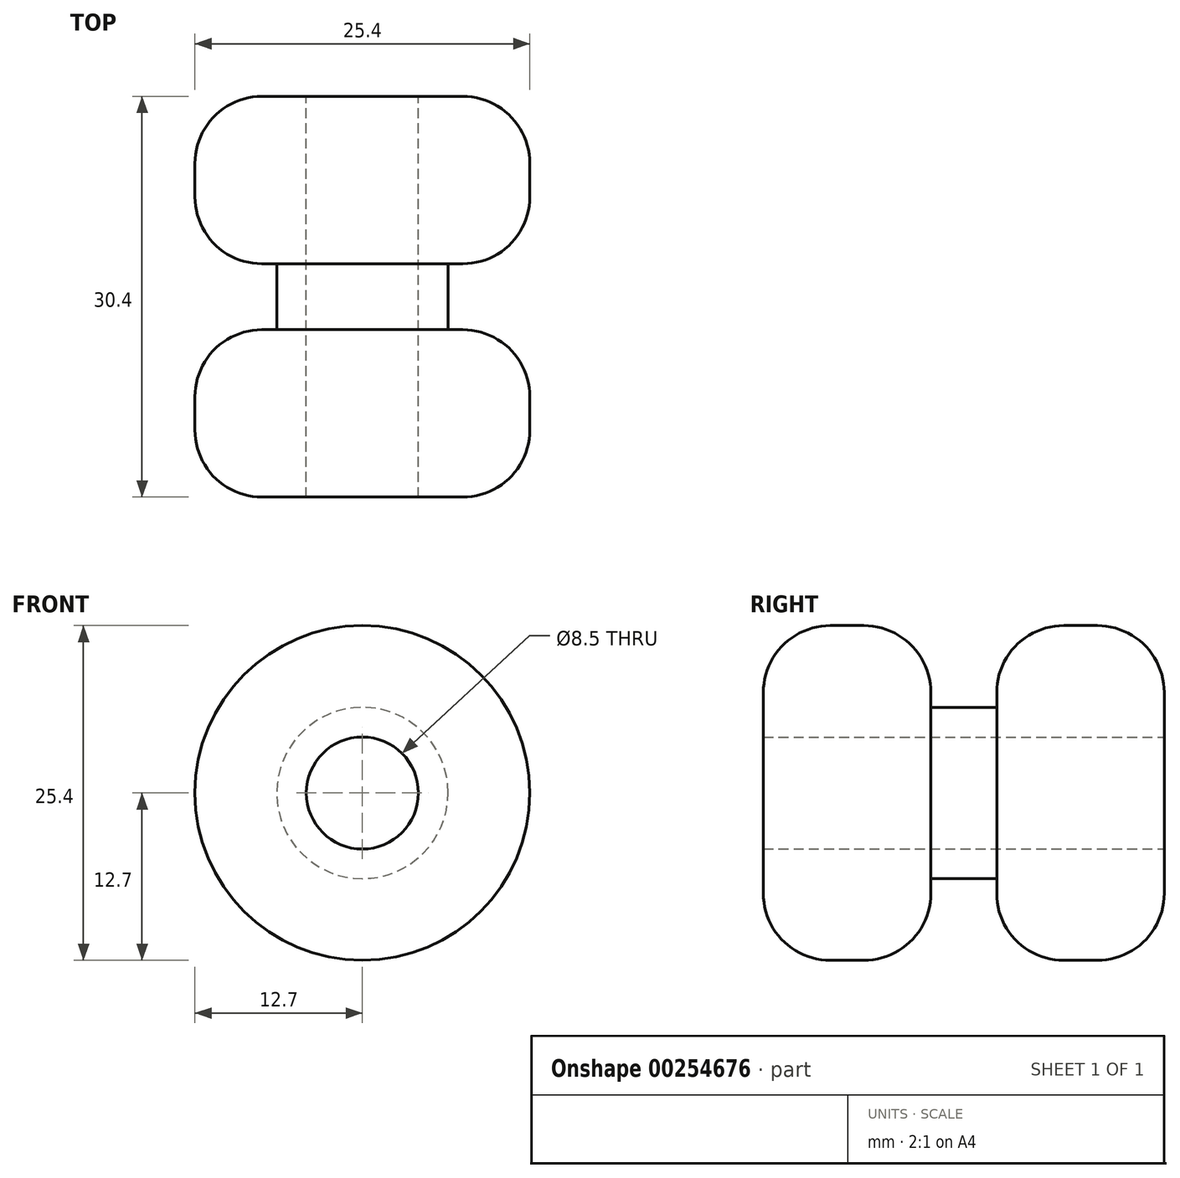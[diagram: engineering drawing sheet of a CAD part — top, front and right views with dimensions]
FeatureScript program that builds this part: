
annotation { "Feature Type Name" : "Feature", "Feature Type Description" : "" }
export const myFeature = defineFeature(function(context is Context, id is Id, definition is map)
    precondition{}
    {
        {
            var Q0;
            Q0=qCreatedBy(makeId("Front.planeOp"),FACE);
            var sketch = newSketch(context, id + "F0", { "sketchPlane" : qUnion([Q0])});
            skCircle(sketch, "E0", {"center": v(0, 0) * mm, "radius": 12.7 * mm});
            skSolve(sketch);
        }
        {
            var Q0;
            Q0 = qSketchRegion(id + "F0", true);
            extrude(context, id + "F1", {"entities" : qUnion([Q0]), "depth" : 12.7 * mm});
        }
        {
            var Q0;
            Q0=makeQuery(id+"F1.opExtrude","CAP_EDGE",EDGE,{"disambiguationData":[OSD([sQuery(id+"F0.wireOp",EDGE,"E0")])],"isStart":true});
            var Q1;
            Q1=makeQuery(id+"F1.opExtrude","CAP_EDGE",EDGE,{"disambiguationData":[OSD([sQuery(id+"F0.wireOp",EDGE,"E0")])],"isStart":false});
            fillet(context, id + "F2", {"entities" : qUnion([Q0, Q1]), "radius" : 5.08 * mm, "tangentPropagation" : true, "allowEdgeOverflow" : false});
        }
        {
            var Q0;
            Q0=qCreatedBy(makeId("Front.planeOp"),FACE);
            var sketch = newSketch(context, id + "F3", { "sketchPlane" : qUnion([Q0])});
            skCircle(sketch, "E1", {"center": v(0, 0) * mm, "radius": 6.5 * mm});
            skSolve(sketch);
        }
        {
            var Q0;
            Q0 = qSketchRegion(id + "F3", true);
            extrude(context, id + "F4", {"entities" : qUnion([Q0]), "operationType" : NewBodyOperationType.ADD, "oppositeDirection" : true, "depth" : 5 * mm});
        }
        {
            var Q0;
            Q0=makeQuery(id+"F4.opExtrude","CAP_FACE",FACE,{"disambiguationData":[OSD([sQuery(id+"F3.wireOp",EDGE,"E1")])],"isStart":false});
            var sketch = newSketch(context, id + "F5", { "sketchPlane" : qUnion([Q0])});
            skCircle(sketch, "E2", {"center": v(0, 0) * mm, "radius": 12.7 * mm});
            skSolve(sketch);
        }
        {
            var Q0;
            Q0 = qSketchRegion(id + "F5", true);
            extrude(context, id + "F6", {"entities" : qUnion([Q0]), "operationType" : NewBodyOperationType.ADD, "depth" : 12.7 * mm});
        }
        {
            var Q0;
            Q0=makeQuery(id+"F6.opExtrude","CAP_EDGE",EDGE,{"disambiguationData":[OSD([sQuery(id+"F5.wireOp",EDGE,"E2")])],"isStart":false});
            var Q1;
            Q1=makeQuery(id+"F6.opExtrude","CAP_EDGE",EDGE,{"disambiguationData":[OSD([sQuery(id+"F5.wireOp",EDGE,"E2")])],"isStart":true});
            fillet(context, id + "F7", {"entities" : qUnion([Q0, Q1]), "radius" : 5.08 * mm, "tangentPropagation" : true, "allowEdgeOverflow" : false});
        }
        {
            var Q0;
            Q0=makeQuery(id+"F6.opExtrude","CAP_FACE",FACE,{"disambiguationData":[OSD([sQuery(id+"F5.wireOp",EDGE,"E2")])],"isStart":false});
            var sketch = newSketch(context, id + "F8", { "sketchPlane" : qUnion([Q0])});
            skPoint(sketch, "E3", {"position": v(0, 0) * mm});
            skSolve(sketch);
        }
        {
            var Q0;
            Q0=sQuery(id+"F8.wireOp",VERTEX,"E3");
            var Q1;
            Q1=makeQuery(id+"F1.opExtrude","SWEPT_BODY",BODY,{"disambiguationData":[OSD([sQuery(id+"F0.wireOp",EDGE,"E0")])]});
            hole(context, id + "F9", {"style" : HoleStyle.SIMPLE, "endStyle" : HoleEndStyle.THROUGH, "holeDiameter" : 8.5 * mm, "tappedDepth" : 12.7 * mm, "tapClearance" : 3, "locations" : qUnion([Q0]), "scope" : qUnion([Q1])});
        }
    });
